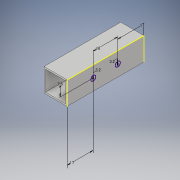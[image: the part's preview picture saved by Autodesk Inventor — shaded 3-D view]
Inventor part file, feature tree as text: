
AUTODESK INVENTOR PART (.ipt)
format: ipt  version: 2019 (Build 230136000, 136)  size: 115,200 bytes
history: native  units: mm
features: sketch x2, other x1, extrude x1
ambient origin geometry x8: Origin, YZ Plane, XZ Plane, XY Plane, X Axis, Y Axis, Z Axis, Center Point
bodies: Body1 (feature_tree)
feature tree (4):
  other  "ソリッド1"
  extrude  "押し出し1"  Depth=15.0mm
  sketch  "スケッチ2"
  sketch  "スケッチ1"
